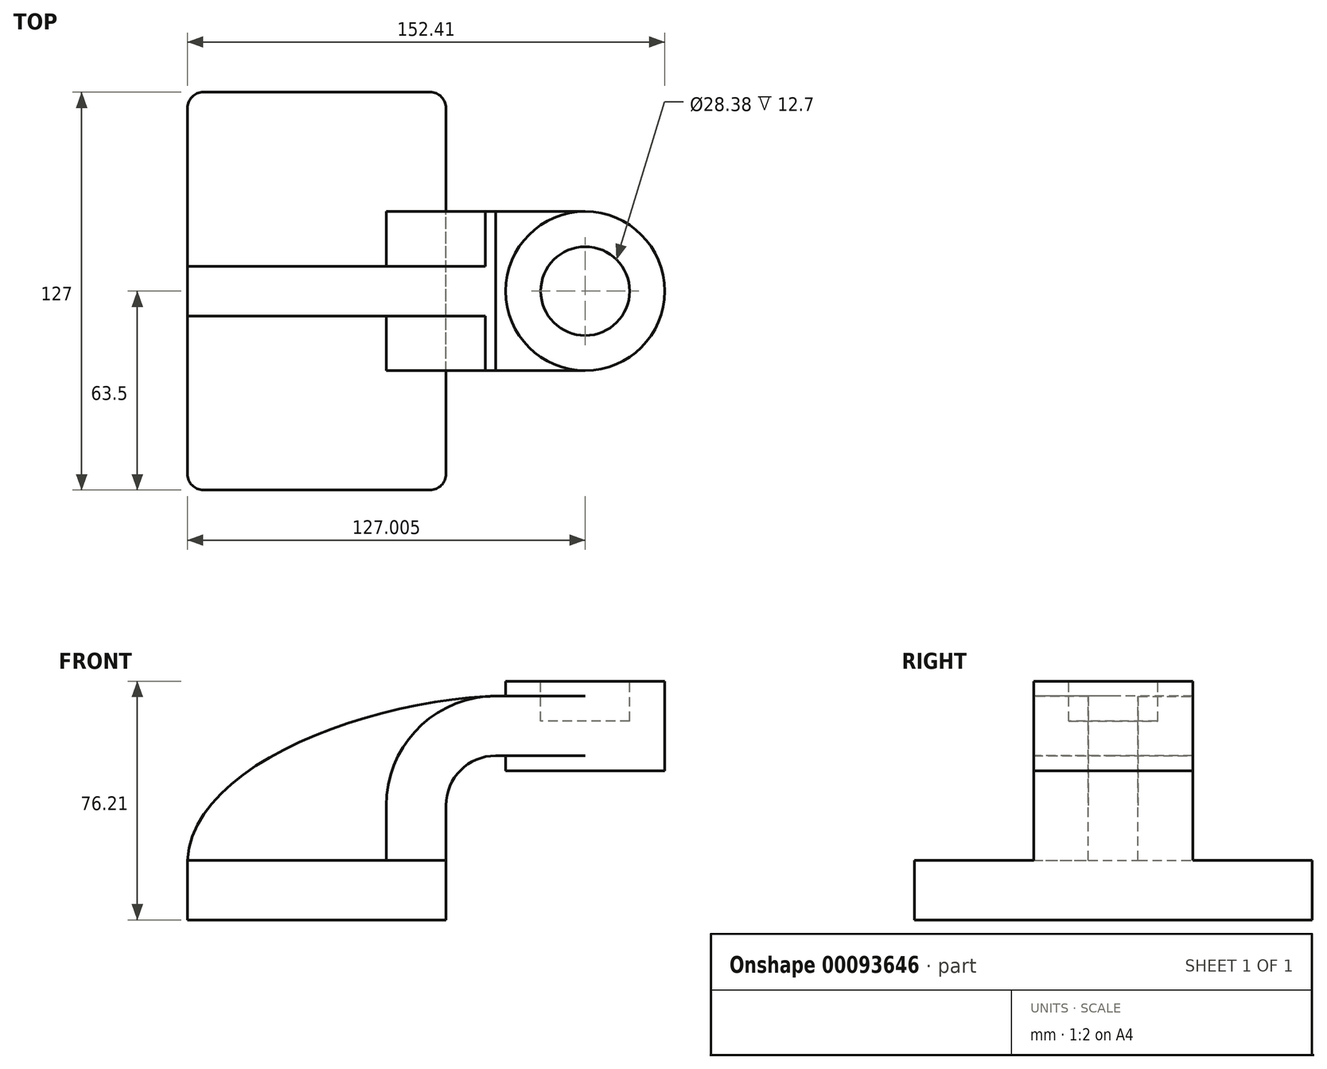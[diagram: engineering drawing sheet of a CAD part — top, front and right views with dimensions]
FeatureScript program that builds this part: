
annotation { "Feature Type Name" : "Feature", "Feature Type Description" : "" }
export const myFeature = defineFeature(function(context is Context, id is Id, definition is map)
    precondition{}
    {
        {
            var Q0;
            Q0=qCreatedBy(makeId("Front.planeOp"),FACE);
            var sketch = newSketch(context, id + "F0", { "sketchPlane" : qUnion([Q0])});
            skLineSegment(sketch, "E0.rect.bottom", {"start": v(-41.28, 9.52) * mm, "end": v(41.28, 9.52) * mm});
            skLineSegment(sketch, "E0.rect.top", {"start": v(-41.28, -9.52) * mm, "end": v(41.28, -9.52) * mm});
            skLineSegment(sketch, "E0.rect.left", {"start": v(-41.28, 9.52) * mm, "end": v(-41.28, -9.52) * mm});
            skLineSegment(sketch, "E0.rect.right", {"start": v(41.28, 9.52) * mm, "end": v(41.28, -9.52) * mm});
            skPoint(sketch, "E0.rect.middle", {"position": v(0, 0) * mm});
            skLineSegment(sketch, "E1", {"start": v(41.28, 9.52) * mm, "end": v(41.28, 27) * mm});
            skArc(sketch, "E2", {"start": v(41.28, 27) * mm, "mid": v(45.92, 38.23) * mm, "end": v(57.15, 42.88) * mm});
            skLineSegment(sketch, "E3", {"start": v(57.15, 42.88) * mm, "end": v(85.72, 42.88) * mm});
            skLineSegment(sketch, "E4.rect.bottom", {"start": v(60.32, 38.1) * mm, "end": v(111.12, 38.1) * mm});
            skLineSegment(sketch, "E4.rect.top", {"start": v(60.32, 66.68) * mm, "end": v(111.12, 66.68) * mm});
            skLineSegment(sketch, "E4.rect.left", {"start": v(60.32, 38.1) * mm, "end": v(60.32, 66.68) * mm});
            skLineSegment(sketch, "E4.rect.right", {"start": v(111.13, 38.1) * mm, "end": v(111.12, 66.68) * mm});
            skPoint(sketch, "E4.rect.middle", {"position": v(85.72, 52.39) * mm});
            skLineSegment(sketch, "E5.0", {"start": v(57.15, 61.93) * mm, "end": v(85.72, 61.93) * mm});
            skArc(sketch, "E5.1", {"start": v(22.23, 27) * mm, "mid": v(32.45, 51.7) * mm, "end": v(57.15, 61.93) * mm});
            skLineSegment(sketch, "E5.2", {"start": v(22.23, 9.52) * mm, "end": v(22.23, 27) * mm});
            skLineSegment(sketch, "E6", {"start": v(85.72, 38.1) * mm, "end": v(85.72, 66.68) * mm});
            skFitSpline(sketch, "E7", {"points": [v(-41.28, 9.53) * mm, v(57.15, 61.93) * mm], "startDerivative": vector(5.2, 92.34) * mm, "endDerivative": vector(120.92, 4.22) * mm});
            skSolve(sketch);
        }
        {
            var Q0;
            Q0=makeQuery(id+"F0.imprint","IMPRINT",FACE,{"disambiguationData":[TD([[makeQuery(id+"F0.imprint","IMPRINT",EDGE,{"derivedFrom":sQuery(id+"F0.wireOp",EDGE,"E0.rect.top")}),1.0]])]});
            extrude(context, id + "F1", {"entities" : qUnion([Q0]), "endBound" : BoundingType.SYMMETRIC, "depth" : 127 * mm});
        }
        {
            var Q0;
            {var subQ9=sQuery(id+"F0.wireOp",EDGE,"E1");Q0=makeQuery(id+"F0.imprint","IMPRINT",FACE,{"disambiguationData":[TD([[makeQuery(id+"F0.imprint","IMPRINT",EDGE,{"derivedFrom":subQ9}),1.0]])]});}
            var Q1;
            {var subQ0=sQuery(id+"F0.wireOp",EDGE,"E6");var subQ1=sQuery(id+"F0.wireOp",EDGE,"E3");var subQ2=makeQuery(id+"F0.imprint","INTERSECT",VERTEX,{"derivedFrom":[subQ1,subQ0]});Q1=makeQuery(id+"F0.imprint","IMPRINT",FACE,{"disambiguationData":[TD([[makeQuery(id+"F0.imprint","IMPRINT",EDGE,{"disambiguationData":[TD([[subQ2,1.0]])],"derivedFrom":subQ1}),1.0]])]});}
            extrude(context, id + "F2", {"entities" : qUnion([Q0, Q1]), "operationType" : NewBodyOperationType.ADD, "endBound" : BoundingType.SYMMETRIC, "depth" : 50.8 * mm});
        }
        {
            var Q0;
            {var subQ3=sQuery(id+"F0.wireOp",EDGE,"E5.2");Q0=makeQuery(id+"F0.imprint","IMPRINT",FACE,{"disambiguationData":[TD([[makeQuery(id+"F0.imprint","IMPRINT",EDGE,{"derivedFrom":subQ3}),1.0]])]});}
            extrude(context, id + "F3", {"entities" : qUnion([Q0]), "operationType" : NewBodyOperationType.ADD, "endBound" : BoundingType.SYMMETRIC, "depth" : 15.88 * mm});
        }
        {
            var Q0;
            {var subQ5=sQuery(id+"F0.wireOp",EDGE,"E4.rect.right");Q0=makeQuery(id+"F0.imprint","IMPRINT",FACE,{"disambiguationData":[TD([[makeQuery(id+"F0.imprint","IMPRINT",EDGE,{"derivedFrom":subQ5}),1.0]])]});}
            var Q1;
            Q1=sQuery(id+"F0.wireOp",EDGE,"E6");
            revolve(context, id + "F4", {"operationType" : NewBodyOperationType.ADD, "entities" : qUnion([Q0]), "axis" : qUnion([Q1]), "revolveType" : RevolveType.FULL});
        }
        {
            var Q0;
            Q0=makeQuery(id+"F1.opExtrude","CAP_EDGE",EDGE,{"disambiguationData":[OSD([sQuery(id+"F0.wireOp",EDGE,"E0.rect.right")])],"isStart":false});
            var Q1;
            Q1=makeQuery(id+"F1.opExtrude","CAP_EDGE",EDGE,{"disambiguationData":[OSD([sQuery(id+"F0.wireOp",EDGE,"E0.rect.left")])],"isStart":false});
            var Q2;
            Q2=makeQuery(id+"F1.opExtrude","CAP_EDGE",EDGE,{"disambiguationData":[OSD([sQuery(id+"F0.wireOp",EDGE,"E0.rect.right")])],"isStart":true});
            var Q3;
            Q3=makeQuery(id+"F1.opExtrude","CAP_EDGE",EDGE,{"disambiguationData":[OSD([sQuery(id+"F0.wireOp",EDGE,"E0.rect.left")])],"isStart":true});
            fillet(context, id + "F5", {"entities" : qUnion([Q0, Q1, Q2, Q3]), "radius" : 5.08 * mm, "tangentPropagation" : true, "allowEdgeOverflow" : false});
        }
        {
            var Q0;
            Q0=makeQuery(id+"F4.opRevolve","SWEPT_FACE",FACE,{"disambiguationData":[OSD([sQuery(id+"F0.wireOp",EDGE,"E4.rect.top")])]});
            var sketch = newSketch(context, id + "F6", { "sketchPlane" : qUnion([Q0])});
            skCircle(sketch, "E8", {"center": v(85.72, 0) * mm, "radius": 14.19 * mm});
            skSolve(sketch);
        }
        {
            var Q0;
            Q0=makeQuery(id+"F6.imprint","IMPRINT",FACE,{"disambiguationData":[TD([[makeQuery(id+"F6.imprint","IMPRINT",EDGE,{"derivedFrom":sQuery(id+"F6.wireOp",EDGE,"E8")}),1.0]])]});
            extrude(context, id + "F7", {"entities" : qUnion([Q0]), "operationType" : NewBodyOperationType.REMOVE, "oppositeDirection" : true, "depth" : 12.7 * mm});
        }
    });
